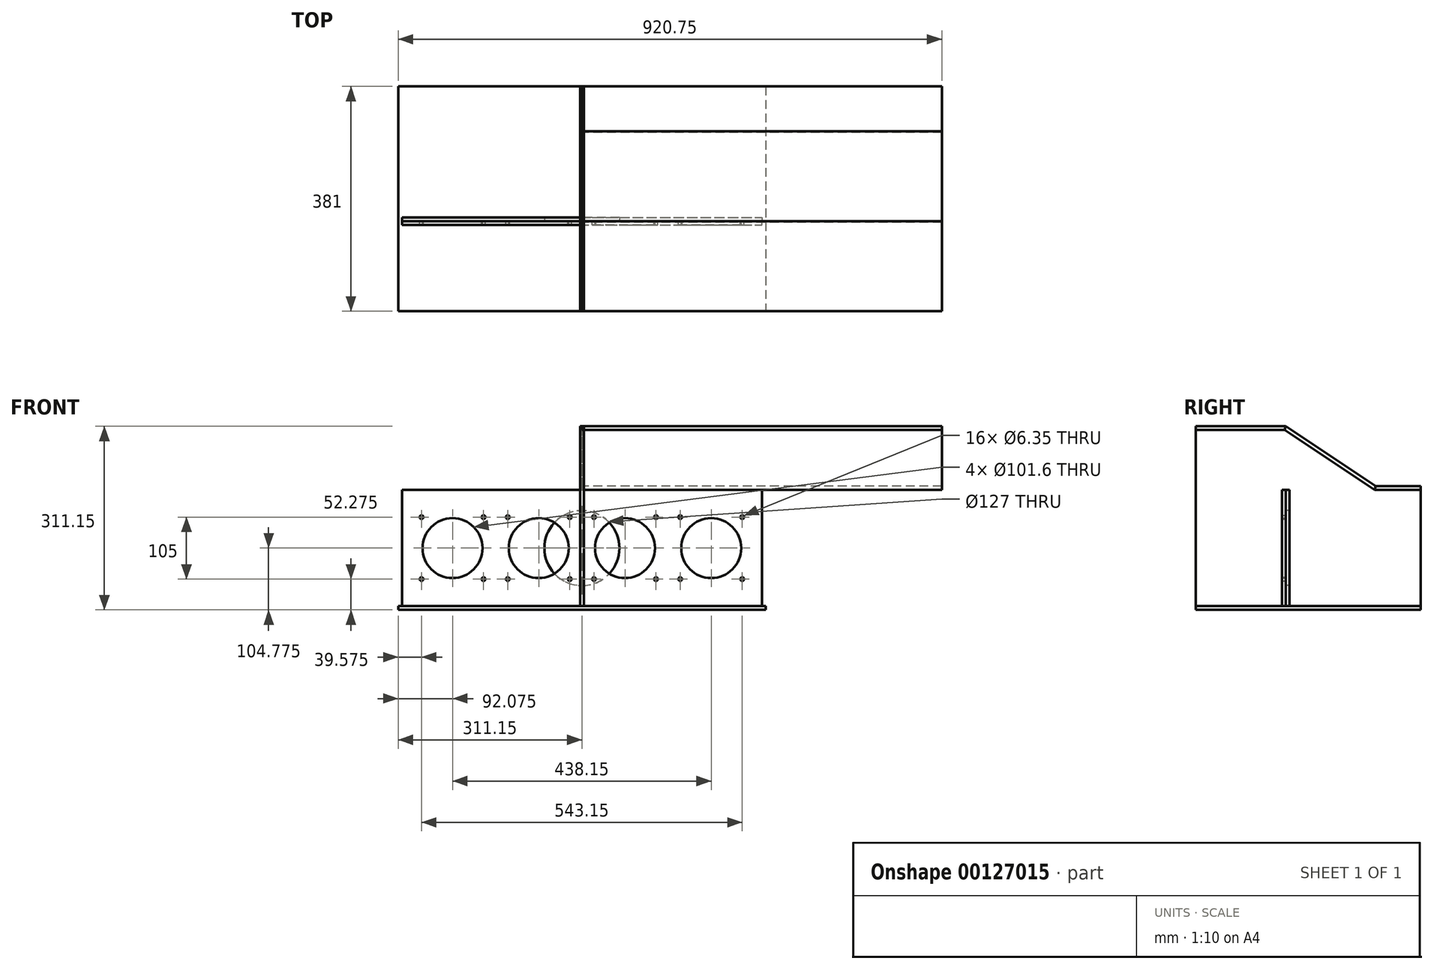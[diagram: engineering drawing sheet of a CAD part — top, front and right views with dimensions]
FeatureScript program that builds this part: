
annotation { "Feature Type Name" : "Feature", "Feature Type Description" : "" }
export const myFeature = defineFeature(function(context is Context, id is Id, definition is map)
    precondition{}
    {
        {
            var Q0;
            Q0=qCreatedBy(makeId("Right.planeOp"),FACE);
            var sketch = newSketch(context, id + "F0", { "sketchPlane" : qUnion([Q0])});
            skLineSegment(sketch, "E0", {"start": v(-152.4, 0) * mm, "end": v(228.6, 0) * mm});
            skLineSegment(sketch, "E1", {"start": v(-152.4, 304.8) * mm, "end": v(-152.4, 0) * mm});
            skLineSegment(sketch, "E2", {"start": v(-152.4, 304.8) * mm, "end": v(0, 304.8) * mm});
            skLineSegment(sketch, "E3", {"start": v(228.6, 203.2) * mm, "end": v(228.6, 0) * mm});
            skLineSegment(sketch, "E4", {"start": v(228.6, 203.2) * mm, "end": v(152.4, 203.2) * mm});
            skLineSegment(sketch, "E5", {"start": v(152.4, 203.2) * mm, "end": v(0, 304.8) * mm});
            skLineSegment(sketch, "E6.0", {"start": v(-152.4, 298.45) * mm, "end": v(-1.92, 298.45) * mm});
            skLineSegment(sketch, "E6.1", {"start": v(150.48, 196.85) * mm, "end": v(-1.92, 298.45) * mm});
            skLineSegment(sketch, "E6.2", {"start": v(228.6, 196.85) * mm, "end": v(150.48, 196.85) * mm});
            skLineSegment(sketch, "E7", {"start": v(152.4, 203.2) * mm, "end": v(150.48, 196.85) * mm});
            skLineSegment(sketch, "E8", {"start": v(0, 304.8) * mm, "end": v(-1.92, 298.45) * mm});
            skSolve(sketch);
        }
        {
            var Q0;
            Q0=makeQuery(id+"F0.imprint","IMPRINT",FACE,{"disambiguationData":[TD([[makeQuery(id+"F0.imprint","IMPRINT",EDGE,{"derivedFrom":sQuery(id+"F0.wireOp",EDGE,"E0")}),1.0]])]});
            var Q1;
            {var subQ0=sQuery(id+"F0.wireOp",EDGE,"sHxgMzo0-4cri-RteF-ppjH-AOB2UVpZnKir");Q1=makeQuery(id+"F0.imprint","IMPRINT",FACE,{"disambiguationData":[TD([[makeQuery(id+"F0.imprint","IMPRINT",EDGE,{"derivedFrom":subQ0}),-1.0]])]});}
            var Q2;
            {var subQ0=sQuery(id+"F0.wireOp",EDGE,"v0GjyCUn-Og30-4AEv-COgM-Bj5hA2AnArNV");Q2=makeQuery(id+"F0.imprint","IMPRINT",FACE,{"disambiguationData":[TD([[makeQuery(id+"F0.imprint","IMPRINT",EDGE,{"derivedFrom":subQ0}),-1.0]])]});}
            var Q3;
            {var subQ0=sQuery(id+"F0.wireOp",EDGE,"XWJ2wI3s-4LZG-JRHq-BLHN-kWdGHjCBwnvl");Q3=makeQuery(id+"F0.imprint","IMPRINT",FACE,{"disambiguationData":[TD([[makeQuery(id+"F0.imprint","IMPRINT",EDGE,{"derivedFrom":subQ0}),1.0]])]});}
            var Q4;
            {var subQ0=sQuery(id+"F0.wireOp",EDGE,"E4");Q4=makeQuery(id+"F0.imprint","IMPRINT",FACE,{"disambiguationData":[TD([[makeQuery(id+"F0.imprint","IMPRINT",EDGE,{"derivedFrom":subQ0}),1.0]])]});}
            var Q5;
            {var subQ0=sQuery(id+"F0.wireOp",EDGE,"E7");Q5=makeQuery(id+"F0.imprint","IMPRINT",FACE,{"disambiguationData":[TD([[makeQuery(id+"F0.imprint","IMPRINT",EDGE,{"derivedFrom":subQ0}),1.0]])]});}
            var Q6;
            Q6=makeQuery(id+"F0.imprint","IMPRINT",FACE,{"disambiguationData":[TD([[makeQuery(id+"F0.imprint","IMPRINT",EDGE,{"derivedFrom":sQuery(id+"F0.wireOp",EDGE,"E5")}),1.0]])]});
            var Q7;
            {var subQ0=sQuery(id+"F0.wireOp",EDGE,"E8");Q7=makeQuery(id+"F0.imprint","IMPRINT",FACE,{"disambiguationData":[TD([[makeQuery(id+"F0.imprint","IMPRINT",EDGE,{"derivedFrom":subQ0}),-1.0]])]});}
            var Q8;
            {var subQ3=sQuery(id+"F0.wireOp",EDGE,"E6.0");Q8=makeQuery(id+"F0.imprint","IMPRINT",FACE,{"disambiguationData":[TD([[makeQuery(id+"F0.imprint","IMPRINT",EDGE,{"derivedFrom":subQ3}),1.0]])]});}
            extrude(context, id + "F1", {"entities" : qUnion([Q0, Q1, Q2, Q3, Q4, Q5, Q6, Q7, Q8]), "endBound" : BoundingType.SYMMETRIC, "depth" : 6.35 * mm});
        }
        {
            var Q0;
            Q0=qCreatedBy(makeId("Top.planeOp"),FACE);
            var sketch = newSketch(context, id + "F2", { "sketchPlane" : qUnion([Q0])});
            skLineSegment(sketch, "E9.bottom", {"start": v(311.15, 228.6) * mm, "end": v(-311.15, 228.6) * mm});
            skLineSegment(sketch, "E9.top", {"start": v(311.15, -152.4) * mm, "end": v(-311.15, -152.4) * mm});
            skLineSegment(sketch, "E9.left", {"start": v(311.15, 228.6) * mm, "end": v(311.15, -152.4) * mm});
            skLineSegment(sketch, "E9.right", {"start": v(-311.15, 228.6) * mm, "end": v(-311.15, -152.4) * mm});
            skPoint(sketch, "E9.middle", {"position": v(0, 0) * mm});
            skSolve(sketch);
        }
        {
            var Q0;
            Q0=makeQuery(id+"F2.imprint","IMPRINT",FACE,{"disambiguationData":[TD([[makeQuery(id+"F2.imprint","IMPRINT",EDGE,{"derivedFrom":sQuery(id+"F2.wireOp",EDGE,"E9.bottom")}),1.0]])]});
            extrude(context, id + "F3", {"entities" : qUnion([Q0]), "oppositeDirection" : true, "depth" : 6.35 * mm});
        }
        {
            var Q0;
            Q0=qCreatedBy(makeId("Front.planeOp"),FACE);
            var sketch = newSketch(context, id + "F4", { "sketchPlane" : qUnion([Q0])});
            skLineSegment(sketch, "E10.bottom", {"start": v(-304.8, 196.85) * mm, "end": v(304.8, 196.85) * mm});
            skLineSegment(sketch, "E10.top", {"start": v(-304.8, 0) * mm, "end": v(304.8, 0) * mm});
            skLineSegment(sketch, "E10.left", {"start": v(-304.8, 196.85) * mm, "end": v(-304.8, 0) * mm});
            skLineSegment(sketch, "E10.right", {"start": v(304.8, 196.85) * mm, "end": v(304.8, 0) * mm});
            skPoint(sketch, "E11", {"position": v(-219.08, 98.43) * mm});
            skPoint(sketch, "E12", {"position": v(-73.03, 98.42) * mm});
            skPoint(sketch, "E13", {"position": v(73.03, 98.42) * mm});
            skPoint(sketch, "E14", {"position": v(219.08, 98.43) * mm});
            skCircle(sketch, "E15", {"center": v(-219.08, 98.43) * mm, "radius": 50.8 * mm});
            skCircle(sketch, "E16", {"center": v(-73.03, 98.42) * mm, "radius": 50.8 * mm});
            skCircle(sketch, "E17", {"center": v(73.03, 98.42) * mm, "radius": 50.8 * mm});
            skCircle(sketch, "E18", {"center": v(219.08, 98.43) * mm, "radius": 50.8 * mm});
            skPoint(sketch, "E19", {"position": v(-271.57, 150.92) * mm});
            skPoint(sketch, "E20", {"position": v(-166.58, 150.92) * mm});
            skPoint(sketch, "E21", {"position": v(-166.58, 45.92) * mm});
            skPoint(sketch, "E22", {"position": v(-271.57, 45.92) * mm});
            skLineSegment(sketch, "E23", {"start": v(-271.57, 150.92) * mm, "end": v(-271.57, 45.92) * mm, "construction": true});
            skLineSegment(sketch, "E24", {"start": v(-166.58, 150.92) * mm, "end": v(-166.58, 45.92) * mm, "construction": true});
            skLineSegment(sketch, "E25", {"start": v(-271.57, 45.92) * mm, "end": v(-166.58, 45.92) * mm, "construction": true});
            skLineSegment(sketch, "E26", {"start": v(-166.58, 150.92) * mm, "end": v(-271.57, 150.92) * mm, "construction": true});
            skLineSegment(sketch, "E27", {"start": v(-219.08, 98.43) * mm, "end": v(-219.08, 196.85) * mm, "construction": true});
            skLineSegment(sketch, "E28", {"start": v(-219.08, 98.43) * mm, "end": v(-219.08, 0) * mm, "construction": true});
            skPoint(sketch, "E29.1.0.0", {"position": v(-125.52, 150.92) * mm});
            skPoint(sketch, "E29.1.0.1", {"position": v(-20.53, 150.92) * mm});
            skPoint(sketch, "E29.1.0.2", {"position": v(-20.53, 45.92) * mm});
            skPoint(sketch, "E29.1.0.3", {"position": v(-125.52, 45.92) * mm});
            skPoint(sketch, "E29.2.0.0", {"position": v(20.53, 150.92) * mm});
            skPoint(sketch, "E29.2.0.1", {"position": v(125.52, 150.92) * mm});
            skPoint(sketch, "E29.2.0.2", {"position": v(125.52, 45.92) * mm});
            skPoint(sketch, "E29.2.0.3", {"position": v(20.53, 45.92) * mm});
            skPoint(sketch, "E29.3.0.0", {"position": v(166.58, 150.92) * mm});
            skPoint(sketch, "E29.3.0.1", {"position": v(271.57, 150.92) * mm});
            skPoint(sketch, "E29.3.0.2", {"position": v(271.57, 45.92) * mm});
            skPoint(sketch, "E29.3.0.3", {"position": v(166.58, 45.92) * mm});
            skLineSegment(sketch, "E29.direction1", {"start": v(-271.57, 45.92) * mm, "end": v(-125.52, 45.92) * mm, "construction": true});
            skLineSegment(sketch, "E30", {"start": v(0, 0) * mm, "end": v(0, 196.85) * mm, "construction": true});
            skLineSegment(sketch, "E31", {"start": v(304.8, 98.42) * mm, "end": v(-304.8, 98.42) * mm, "construction": true});
            skCircle(sketch, "E32", {"center": v(0, 98.42) * mm, "radius": 63.5 * mm});
            skSolve(sketch);
        }
        {
            var Q0;
            {var subQ0=sQuery(id+"F4.wireOp",EDGE,"E32");var subQ1=sQuery(id+"F4.wireOp",EDGE,"E16");var subQ2=makeQuery(id+"F4.imprint","INTERSECT",VERTEX,{"disambiguationData":[OD(0.0)],"derivedFrom":[subQ1,subQ0]});Q0=makeQuery(id+"F4.imprint","IMPRINT",FACE,{"disambiguationData":[TD([[makeQuery(id+"F4.imprint","IMPRINT",EDGE,{"disambiguationData":[TD([[subQ2,-1.0]])],"derivedFrom":subQ1}),1.0]])]});}
            var Q1;
            Q1=makeQuery(id+"F4.imprint","IMPRINT",FACE,{"disambiguationData":[TD([[makeQuery(id+"F4.imprint","IMPRINT",EDGE,{"derivedFrom":sQuery(id+"F4.wireOp",EDGE,"E10.bottom")}),-1.0]])]});
            var Q2;
            Q2=makeQuery(id+"F4.imprint","IMPRINT",FACE,{"disambiguationData":[TD([[makeQuery(id+"F4.imprint","IMPRINT",EDGE,{"derivedFrom":sQuery(id+"F4.wireOp",EDGE,"E15")}),1.0]])]});
            var Q3;
            Q3=makeQuery(id+"F4.imprint","IMPRINT",FACE,{"disambiguationData":[TD([[makeQuery(id+"F4.imprint","IMPRINT",EDGE,{"derivedFrom":sQuery(id+"F4.wireOp",EDGE,"E18")}),1.0]])]});
            var Q4;
            {var subQ0=sQuery(id+"F4.wireOp",EDGE,"E32");var subQ1=sQuery(id+"F4.wireOp",EDGE,"E17");var subQ2=makeQuery(id+"F4.imprint","INTERSECT",VERTEX,{"disambiguationData":[OD(0.0)],"derivedFrom":[subQ1,subQ0]});Q4=makeQuery(id+"F4.imprint","IMPRINT",FACE,{"disambiguationData":[TD([[makeQuery(id+"F4.imprint","IMPRINT",EDGE,{"disambiguationData":[TD([[subQ2,1.0]])],"derivedFrom":subQ1}),1.0]])]});}
            extrude(context, id + "F5", {"entities" : qUnion([Q0, Q1, Q2, Q3, Q4]), "oppositeDirection" : true, "depth" : 6.35 * mm});
        }
        {
            var Q0;
            {var subQ0=sQuery(id+"F0.wireOp",EDGE,"E2");Q0=makeQuery(id+"F0.imprint","IMPRINT",FACE,{"disambiguationData":[TD([[makeQuery(id+"F0.imprint","IMPRINT",EDGE,{"derivedFrom":subQ0}),-1.0]])]});}
            extrude(context, id + "F6", {"entities" : qUnion([Q0]), "depth" : 609.6 * mm});
        }
        {
            var Q0;
            Q0=makeQuery(id+"F0.imprint","IMPRINT",FACE,{"disambiguationData":[TD([[makeQuery(id+"F0.imprint","IMPRINT",EDGE,{"derivedFrom":sQuery(id+"F0.wireOp",EDGE,"E5")}),1.0]])]});
            extrude(context, id + "F7", {"entities" : qUnion([Q0]), "depth" : 609.6 * mm});
        }
        {
            var Q0;
            {var subQ0=sQuery(id+"F0.wireOp",EDGE,"E4");Q0=makeQuery(id+"F0.imprint","IMPRINT",FACE,{"disambiguationData":[TD([[makeQuery(id+"F0.imprint","IMPRINT",EDGE,{"derivedFrom":subQ0}),1.0]])]});}
            extrude(context, id + "F8", {"entities" : qUnion([Q0]), "depth" : 609.6 * mm});
        }
        {
            var Q0;
            Q0=makeQuery(id+"F4.imprint","IMPRINT",FACE,{"disambiguationData":[TD([[makeQuery(id+"F4.imprint","IMPRINT",EDGE,{"derivedFrom":sQuery(id+"F4.wireOp",EDGE,"E10.bottom")}),-1.0]])]});
            var Q1;
            {var subQ0=sQuery(id+"F4.wireOp",EDGE,"E32");var subQ1=sQuery(id+"F4.wireOp",EDGE,"E16");var subQ2=makeQuery(id+"F4.imprint","INTERSECT",VERTEX,{"disambiguationData":[OD(0.0)],"derivedFrom":[subQ1,subQ0]});Q1=makeQuery(id+"F4.imprint","IMPRINT",FACE,{"disambiguationData":[TD([[makeQuery(id+"F4.imprint","IMPRINT",EDGE,{"disambiguationData":[TD([[subQ2,1.0]])],"derivedFrom":subQ1}),-1.0]])]});}
            extrude(context, id + "F9", {"entities" : qUnion([Q0, Q1]), "depth" : 6.35 * mm});
        }
        {
            var Q0;
            Q0=sQuery(id+"F4.wireOp",VERTEX,"E19");
            var Q1;
            Q1=sQuery(id+"F4.wireOp",VERTEX,"E20");
            var Q2;
            Q2=sQuery(id+"F4.wireOp",VERTEX,"E29.1.0.0");
            var Q3;
            Q3=sQuery(id+"F4.wireOp",VERTEX,"E29.1.0.3");
            var Q4;
            Q4=sQuery(id+"F4.wireOp",VERTEX,"E21");
            var Q5;
            Q5=sQuery(id+"F4.wireOp",VERTEX,"E22");
            var Q6;
            Q6=sQuery(id+"F4.wireOp",VERTEX,"E29.1.0.1");
            var Q7;
            Q7=sQuery(id+"F4.wireOp",VERTEX,"E29.2.0.0");
            var Q8;
            Q8=sQuery(id+"F4.wireOp",VERTEX,"E29.1.0.2");
            var Q9;
            Q9=sQuery(id+"F4.wireOp",VERTEX,"E29.2.0.3");
            var Q10;
            Q10=sQuery(id+"F4.wireOp",VERTEX,"E29.2.0.1");
            var Q11;
            Q11=sQuery(id+"F4.wireOp",VERTEX,"E29.3.0.0");
            var Q12;
            Q12=sQuery(id+"F4.wireOp",VERTEX,"E29.3.0.1");
            var Q13;
            Q13=sQuery(id+"F4.wireOp",VERTEX,"E29.3.0.2");
            var Q14;
            Q14=sQuery(id+"F4.wireOp",VERTEX,"E29.3.0.3");
            var Q15;
            Q15=sQuery(id+"F4.wireOp",VERTEX,"E29.2.0.2");
            var Q16;
            Q16=makeQuery(id+"F9.opExtrude","SWEPT_BODY",BODY,{"disambiguationData":[OSD([sQuery(id+"F4.wireOp",EDGE,"E10.bottom"),sQuery(id+"F4.wireOp",EDGE,"E10.top"),sQuery(id+"F4.wireOp",EDGE,"E10.left"),sQuery(id+"F4.wireOp",EDGE,"E10.right"),sQuery(id+"F4.wireOp",EDGE,"E15"),sQuery(id+"F4.wireOp",EDGE,"E16"),sQuery(id+"F4.wireOp",EDGE,"E17"),sQuery(id+"F4.wireOp",EDGE,"E18")])]});
            hole(context, id + "F10", {"style" : HoleStyle.SIMPLE, "endStyle" : HoleEndStyle.THROUGH, "oppositeDirection" : true, "holeDiameter" : 6.35 * mm, "locations" : qUnion([Q0, Q1, Q2, Q3, Q4, Q5, Q6, Q7, Q8, Q9, Q10, Q11, Q12, Q13, Q14, Q15]), "scope" : qUnion([Q16]), "isTappedThrough" : true});
        }
    });
